# Revit family: 1414004 - Shadow Surface 220
name_source: partatom
category: Lighting Fixtures
revit_build: Autodesk Revit 2018 (Build: 20170223_1515(x64)
units: mm (PartAtom-declared; Revit-internal decimal feet)

## family parameters
Always vertical = Yes
Cut with Voids When Loaded = No
Host = Ceiling
Light Source = No
OmniClass Number = 23.80.70.11
OmniClass Title = Luminaries for Internal Lighting
Part Type = Normal
Room Calculation Point = No
Round Connector Dimension = Use Diameter
Shared = No

## types (2) — shared parameters
Apparent Load = 0 VA
Manufacturer URL - Europe and Rest of World = www.astrolighting.com
Manufacturer URL - North America = us.astrolighting.com
Product CCT = 2700K / 3000K

## per-type parameters (varying)
| type | ADA compliant | Dimmable | Dimming Method | Driver Included | Driver Required | Efficacy (lm/w) | Electrical Class | Lamp | Length of supplied cable | Light Source Fixed | Location / IP Rating | Main Finish | Main Material | Max Drop (pendants) | Power (Watts) | Product CRI | Product Dimensions (MM) | Product Location | Product Name | Product SKU | Product Weight (KG) | Wattage Comments |
| CE | Not Applicable | Yes | Lamp Dependent | Not Applicable | No | Lamp Dependent | 1 | GU10 - LED | Not Applicable | Yes | IP20 | Plaster | Plaster | Not Applicable | Lamp Dependent | 80 / 90 | 220 x 82 x 86 | Indoor | Shadow Surface 220 | 1414004 | 1 mm  [stored 0.00328084 ft] | 6W Max |
| ETL |  |  |  |  |  |  |  |  |  |  |  |  |  |  |  | 80/ 90 |  |  |  | 1234567 | 0 mm  [stored 0 ft] |  |

note: [stored X ft] marks values corroborated as IEEE doubles in the binary element streams (Revit-internal decimal feet)

## geometry (parser evidence)
native form markers: Sweep x2
no freeform markers — native parametric forms only
